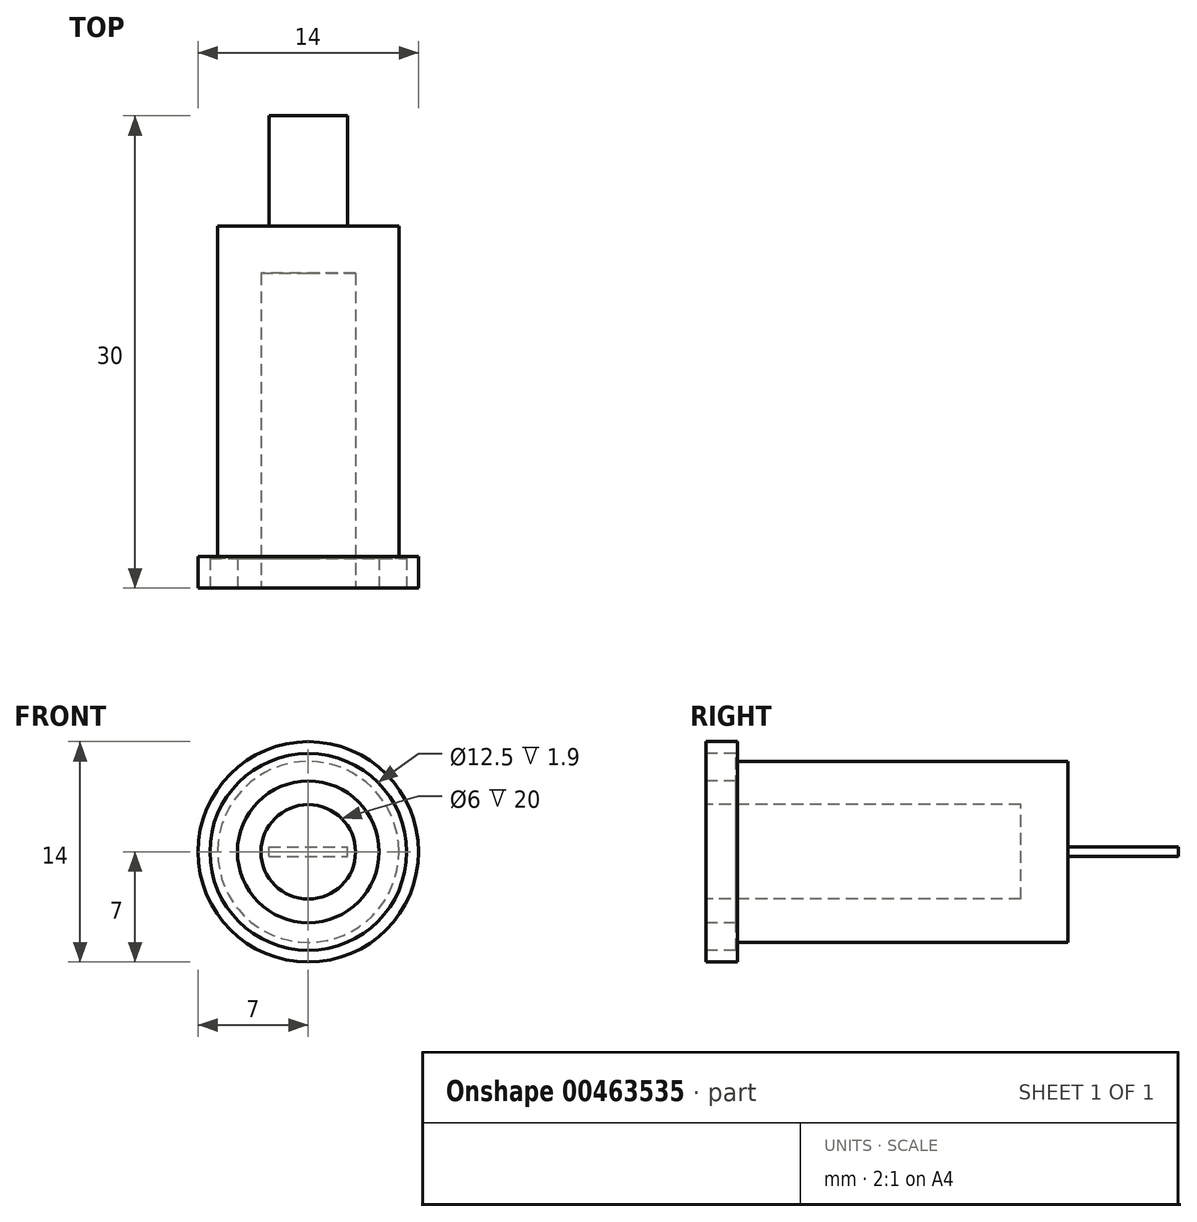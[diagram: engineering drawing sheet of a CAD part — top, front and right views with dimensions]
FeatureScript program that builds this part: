
annotation { "Feature Type Name" : "Feature", "Feature Type Description" : "" }
export const myFeature = defineFeature(function(context is Context, id is Id, definition is map)
    precondition{}
    {
        {
            var Q0;
            Q0=qCreatedBy(makeId("Front.planeOp"),FACE);
            var sketch = newSketch(context, id + "F0", { "sketchPlane" : qUnion([Q0])});
            skCircle(sketch, "E0", {"center": v(0, 0) * mm, "radius": 7 * mm});
            skSolve(sketch);
        }
        {
            var Q0;
            Q0 = qSketchRegion(id + "F0", true);
            extrude(context, id + "F1", {"entities" : qUnion([Q0]), "oppositeDirection" : true, "depth" : 2 * mm, "offsetDistance" : 25 * mm});
        }
        {
            var Q0;
            Q0=makeQuery(id+"F1.opExtrude","CAP_FACE",FACE,{"disambiguationData":[OSD([sQuery(id+"F0.wireOp",EDGE,"E0")])],"isStart":false});
            var sketch = newSketch(context, id + "F2", { "sketchPlane" : qUnion([Q0])});
            skCircle(sketch, "E1", {"center": v(0, 0) * mm, "radius": 5.75 * mm});
            skSolve(sketch);
        }
        {
            var Q0;
            Q0 = qSketchRegion(id + "F2", true);
            extrude(context, id + "F3", {"entities" : qUnion([Q0]), "operationType" : NewBodyOperationType.ADD, "depth" : 21 * mm, "offsetDistance" : 25 * mm});
        }
        {
            var Q0;
            Q0=makeQuery(id+"F1.opExtrude","CAP_FACE",FACE,{"disambiguationData":[OSD([sQuery(id+"F0.wireOp",EDGE,"E0")])],"isStart":true});
            var sketch = newSketch(context, id + "F4", { "sketchPlane" : qUnion([Q0])});
            skCircle(sketch, "E2", {"center": v(0, 0) * mm, "radius": 3 * mm});
            skSolve(sketch);
        }
        {
            var Q0;
            Q0 = qSketchRegion(id + "F4", true);
            extrude(context, id + "F5", {"entities" : qUnion([Q0]), "operationType" : NewBodyOperationType.REMOVE, "oppositeDirection" : true, "depth" : 20 * mm, "offsetDistance" : 25 * mm});
        }
        {
            var Q0;
            Q0=makeQuery(id+"F1.opExtrude","CAP_FACE",FACE,{"disambiguationData":[OSD([sQuery(id+"F0.wireOp",EDGE,"E0")])],"isStart":true});
            var sketch = newSketch(context, id + "F6", { "sketchPlane" : qUnion([Q0])});
            skCircle(sketch, "E3", {"center": v(0, 0) * mm, "radius": 4.5 * mm});
            skCircle(sketch, "E4", {"center": v(0, 0) * mm, "radius": 6.25 * mm});
            skSolve(sketch);
        }
        {
            var Q0;
            Q0 = qSketchRegion(id + "F6", true);
            extrude(context, id + "F7", {"entities" : qUnion([Q0]), "operationType" : NewBodyOperationType.REMOVE, "oppositeDirection" : true, "depth" : 1.9 * mm, "offsetDistance" : 25 * mm});
        }
        {
            var Q0;
            Q0=qCreatedBy(makeId("Top.planeOp"),FACE);
            var sketch = newSketch(context, id + "F8", { "sketchPlane" : qUnion([Q0])});
            skLineSegment(sketch, "E5.bottom", {"start": v(2.5, 22) * mm, "end": v(-2.5, 22) * mm});
            skLineSegment(sketch, "E5.top", {"start": v(2.5, 30) * mm, "end": v(-2.5, 30) * mm});
            skLineSegment(sketch, "E5.left", {"start": v(2.5, 22) * mm, "end": v(2.5, 30) * mm});
            skLineSegment(sketch, "E5.right", {"start": v(-2.5, 22) * mm, "end": v(-2.5, 30) * mm});
            skPoint(sketch, "E5.middle", {"position": v(0, 26) * mm});
            skSolve(sketch);
        }
        {
            var Q0;
            Q0 = qSketchRegion(id + "F8", true);
            extrude(context, id + "F9", {"entities" : qUnion([Q0]), "operationType" : NewBodyOperationType.ADD, "depth" : .6 * mm, "offsetDistance" : 25 * mm, "symmetric" : true});
        }
    });
